# Revit family: Reduzierstück
name_source: partatom
category: HLS-Bauteile
revit_build: Autodesk Revit 2017 (Build: 20190507_1515(x64)
units: mm (PartAtom-declared; Revit-internal decimal feet)

## family parameters
Arbeitsebenenbasiert = Ja
Beim Laden mit Abzugskörper schneiden = Nein
Bemaßung runder Anschluss = Durchmesser verwenden
Gemeinsam genutzt = Ja
Immer vertikal = Nein
Raumberechnungspunkt = Nein
Teiletyp = Normal

## types (7) — shared parameters
Fabrikat = MEFA
Firma = MEFA Befestigungs- und Montagesysteme GmbH
Kurztext1 = Reduzierstück sechskant
Material = Stahl
Mengeneinheit = St
Oberflaeche = galvanisch verzinkt
Vorgabe-Ansicht = 1219 mm

## per-type parameters (varying)
| type | Artikelnummer | Außengewinde | D | EAN | F2 | Gewicht | Gewicht pro Bauteil | H | Innengewinde 1 | Kurztext2 | L1 | L2 | Lochung | Länge | Länge Außengewinde | Länge Innengewinde 1 | Schlüsselweite | vpe |
| Reduzierstück sechskant IG M 8- AG M10 | 0725528 | M10 | 8 mm  [stored 0.0262467 ft] | 4250928416384 | 7 mm  [stored 0.0229659 ft] | 0.02 kg | 0.02 kg | 13 mm | M8 | Innengew. M8 Außengewinde M10 L=21 mm | 8 mm  [stored 0.0262467 ft] | 8 mm  [stored 0.0262467 ft] | 7 mm  [stored 0.0229659 ft] | 21 mm  [stored 0.0688976 ft] | 8 mm | 8 mm | 13 | 100 St |
| Reduzierstück sechskant IG M10- AG M 8 | 0720518 | M8 | 7 mm  [stored 0.0229659 ft] | 4250928416377 | 7 mm  [stored 0.0229659 ft] | 0.02 kg | 0.02 kg | 13 mm | M10 | Innengew. M10 Außengewinde M8 L=23 mm | 8 mm  [stored 0.0262467 ft] | 10 mm  [stored 0.0328084 ft] | 9 mm | 23 mm  [stored 0.0754593 ft] | 8 mm | 10 mm | 13 | 100 St |
| Reduzierstück sechskant IG M10- AG M12 | 0720496 | M12 | 10 mm  [stored 0.0328084 ft] | 4250928416360 | 7 mm  [stored 0.0229659 ft] | 0.02 kg | 0.02 kg | 13 mm | M10 | Innengew. M10 Außengewinde M12 L=23 mm | 10 mm  [stored 0.0328084 ft] | 10 mm  [stored 0.0328084 ft] | 9 mm | 23 mm  [stored 0.0754593 ft] | 10 mm | 10 mm | 13 | 100 St |
| Reduzierstück sechskant IG M12- AG M10 | 0720011 | M10 | 8 mm  [stored 0.0262467 ft] | 4250928416353 | 9 mm | 0.03 kg | 0.03 kg | 15 mm  [stored 0.0492126 ft] | M12 | Innengew. M12 Außengewinde M10 L=25 mm | 10 mm  [stored 0.0328084 ft] | 10 mm  [stored 0.0328084 ft] | 10 mm  [stored 0.0328084 ft] | 25 mm  [stored 0.082021 ft] | 10 mm | 10 mm | 17 | 100 St |
| Reduzierstück sechskant IG M16- AG M12 | 0726508 | M12 | 10 mm  [stored 0.0328084 ft] | 4250928416391 | 12 mm  [stored 0.0393701 ft] | 0.07 kg | 0.07 kg | 14 mm  [stored 0.0459318 ft] | M16 | Innengew. M16 Außengewinde M12 L=32 mm | 10 mm  [stored 0.0328084 ft] | 15 mm  [stored 0.0492126 ft] | 14 mm  [stored 0.0459318 ft] | 32 mm  [stored 0.104987 ft] | 10 mm | 15 mm | 24 | 50 St |
| Reduzierstück sechskant IG 1/2"- AG M12 | 0726509 | M12 | 10 mm  [stored 0.0328084 ft] | 4250928416407 | 15 mm  [stored 0.0492126 ft] | 0.05 kg | 0.05 kg | 25 mm  [stored 0.082021 ft] | 1/2'' | Innengew. 1/2'' Außengewinde M12 L=29 mm | 10 mm  [stored 0.0328084 ft] | 15 mm  [stored 0.0492126 ft] | 21 mm  [stored 0.0688976 ft] | 29 mm  [stored 0.0951444 ft] |  |  | 24 | 50 St |
| Reduzierstück sechskant IG 1/2"- AG M16 | 0726510 | M16 | 14 mm  [stored 0.0459318 ft] | 4250928416414 | 15 mm  [stored 0.0492126 ft] | 0.12 kg | 0.12 kg | 25 mm  [stored 0.082021 ft] | 1/2'' | Innengew. 1/2'' Außengewinde M16 L=35 mm | 10 mm  [stored 0.0328084 ft] | 15 mm  [stored 0.0492126 ft] | 21 mm  [stored 0.0688976 ft] | 35 mm  [stored 0.114829 ft] |  |  | 30 | 25 St |

note: [stored X ft] marks values corroborated as IEEE doubles in the binary element streams (Revit-internal decimal feet)

## geometry (parser evidence)
native form markers: Sweep x3
no freeform markers — native parametric forms only
